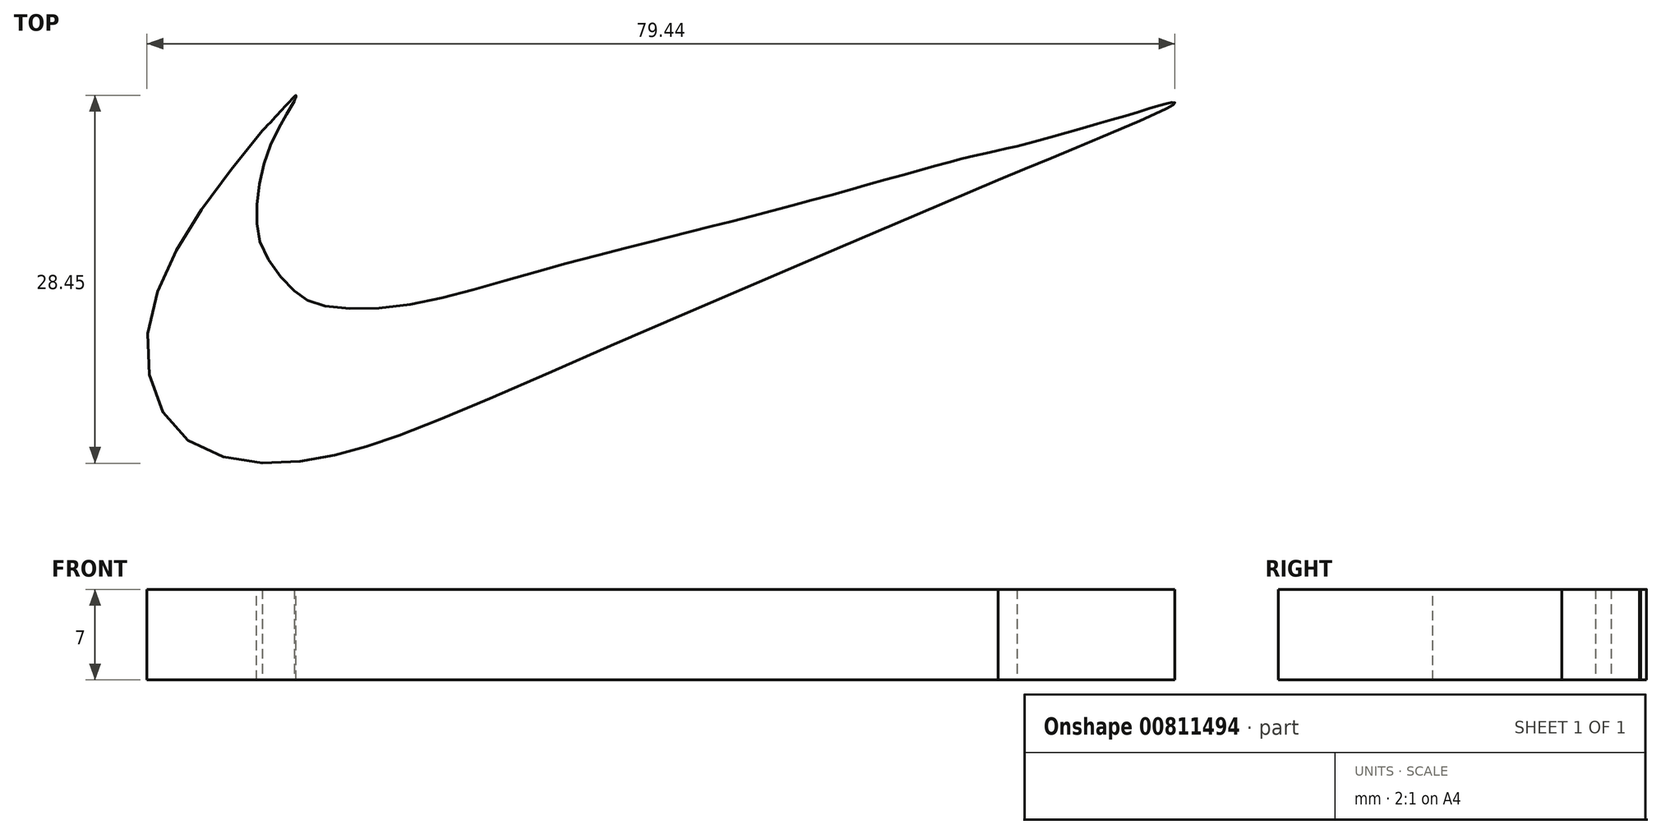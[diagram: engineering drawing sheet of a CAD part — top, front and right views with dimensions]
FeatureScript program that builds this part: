
annotation { "Feature Type Name" : "Feature", "Feature Type Description" : "" }
export const myFeature = defineFeature(function(context is Context, id is Id, definition is map)
    precondition{}
    {
        {
            var Q0;
            Q0=qCreatedBy(makeId("Top.planeOp"),FACE);
            var sketch = newSketch(context, id + "F0", { "sketchPlane" : qUnion([Q0])});
            skFitSpline(sketch, "E0", {"points": [v(-24.54, 7.99) * mm, v(-25.59, 6.15) * mm, v(-26.85, 3.26) * mm, v(-27.43, -0.4) * mm, v(-27, -3.37) * mm, v(-24.83, -6.41) * mm, v(-22.7, -7.73) * mm, v(-16.28, -7.83) * mm, v(-7.26, -5.6) * mm, v(1.16, -3.35) * mm], "startDerivative": vector(-13.34, -22.64) * mm, "endDerivative": vector(53.4, 13.78) * mm});
            skFitSpline(sketch, "E1", {"points": [v(1.16, -3.35) * mm, v(16.6, 0.63) * mm, v(26.8, 3.46) * mm, v(31.32, 4.5) * mm], "startDerivative": vector(37.5, 9.4) * mm, "endDerivative": vector(18, 3.82) * mm});
            skFitSpline(sketch, "E2", {"points": [v(31.32, 4.5) * mm, v(40.47, 7.08) * mm, v(43.35, 7.88) * mm, v(43.52, 7.84) * mm, v(29.85, 1.88) * mm], "startDerivative": vector(29.7, 8.2) * mm, "endDerivative": vector(-48.04, -19.82) * mm});
            skFitSpline(sketch, "E3", {"points": [v(29.85, 1.88) * mm, v(0.14, -10.83) * mm, v(-15.33, -17.45) * mm, v(-20.7, -19.2) * mm, v(-26.56, -20) * mm, v(-33.1, -17.95) * mm, v(-35.91, -11.7) * mm, v(-33.54, -3.35) * mm, v(-27, 5.7) * mm], "startDerivative": vector(-144.2, -61.26) * mm, "endDerivative": vector(56.65, 69.51) * mm});
            skFitSpline(sketch, "E4", {"points": [v(-27, 5.7) * mm, v(-24.69, 8.17) * mm, v(-24.4, 8.43) * mm, v(-24.54, 7.99) * mm], "startDerivative": vector(4.7, 5.05) * mm, "endDerivative": vector(-1.14, -2.86) * mm});
            skSolve(sketch);
        }
        {
            var Q0;
            Q0=makeQuery(id+"F0.imprint","IMPRINT",FACE,{"disambiguationData":[TD([[makeQuery(id+"F0.imprint","IMPRINT",EDGE,{"derivedFrom":sQuery(id+"F0.wireOp",EDGE,"E0")}),-1.0]])]});
            extrude(context, id + "F1", {"entities" : qUnion([Q0]), "depth" : 7 * mm, "offsetDistance" : 25 * mm});
        }
    });
